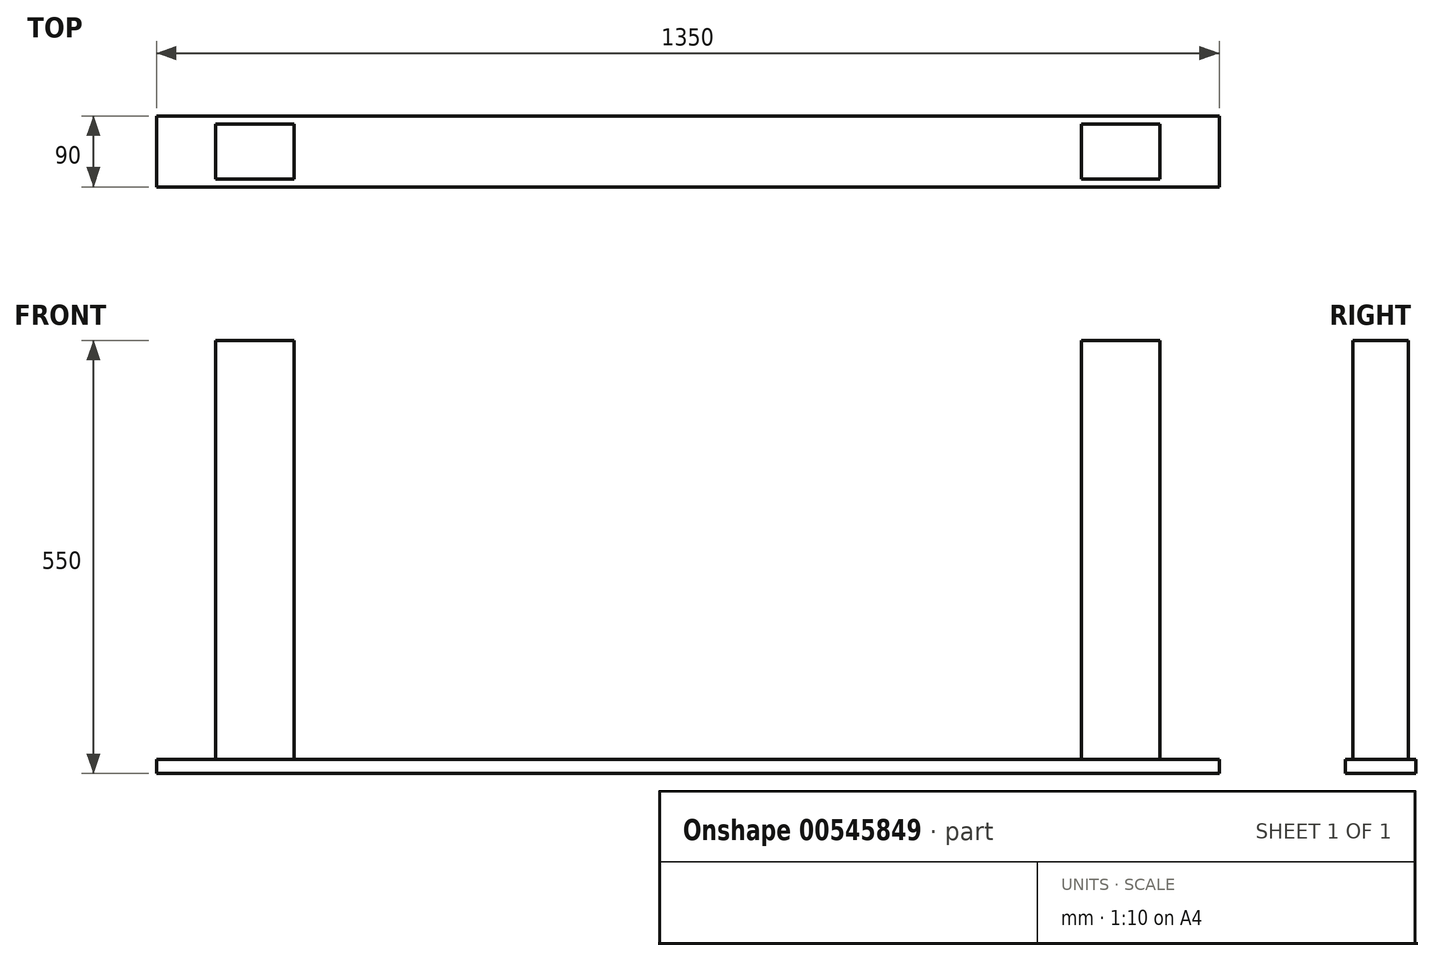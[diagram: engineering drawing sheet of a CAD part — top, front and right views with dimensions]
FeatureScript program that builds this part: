
annotation { "Feature Type Name" : "Feature", "Feature Type Description" : "" }
export const myFeature = defineFeature(function(context is Context, id is Id, definition is map)
    precondition{}
    {
        {
            var Q0;
            Q0=qCreatedBy(makeId("Top.planeOp"),FACE);
            var sketch = newSketch(context, id + "F0", { "sketchPlane" : qUnion([Q0])});
            skLineSegment(sketch, "E0", {"start": v(0, 0) * mm, "end": v(0, -1700) * mm, "construction": true});
            skLineSegment(sketch, "E1", {"start": v(-675, 0) * mm, "end": v(0, 0) * mm, "construction": true});
            skLineSegment(sketch, "E2", {"start": v(-675, -1350) * mm, "end": v(-675, -1700) * mm, "construction": true});
            skLineSegment(sketch, "E3", {"start": v(-675, -1700) * mm, "end": v(-425, -1700) * mm, "construction": true});
            skLineSegment(sketch, "E4.MirrorCS", {"start": v(675, 0) * mm, "end": v(0, 0) * mm, "construction": true});
            skLineSegment(sketch, "E5", {"start": v(-425, -1700) * mm, "end": v(-675, -1350) * mm, "construction": true});
            skLineSegment(sketch, "E6", {"start": v(675, 0) * mm, "end": v(675, -1350) * mm, "construction": true});
            skLineSegment(sketch, "E7", {"start": v(425, -1700) * mm, "end": v(-425, -1700) * mm, "construction": true});
            skLineSegment(sketch, "E8", {"start": v(675, -1350) * mm, "end": v(425, -1700) * mm, "construction": true});
            skLineSegment(sketch, "E9", {"start": v(-675, -1350) * mm, "end": v(-675, 0) * mm, "construction": true});
            skLineSegment(sketch, "E10", {"start": v(-675, -650) * mm, "end": v(675, -650) * mm, "construction": true});
            skLineSegment(sketch, "E11.bottom", {"start": v(-675, -325) * mm, "end": v(675, -325) * mm});
            skLineSegment(sketch, "E11.left", {"start": v(-675, -325) * mm, "end": v(-675, -415) * mm});
            skLineSegment(sketch, "E11.right", {"start": v(675, -325) * mm, "end": v(675, -650) * mm});
            skLineSegment(sketch, "E12", {"start": v(-675, -415) * mm, "end": v(675, -415) * mm});
            skLineSegment(sketch, "E13", {"start": v(675, -415) * mm, "end": v(675, -325) * mm});
            skSolve(sketch);
        }
        {
            var Q0;
            Q0=makeQuery(id+"F0.imprint","IMPRINT",FACE,{"disambiguationData":[TD([[makeQuery(id+"F0.imprint","IMPRINT",EDGE,{"derivedFrom":sQuery(id+"F0.wireOp",EDGE,"E11.bottom")}),-1.0]])]});
            extrude(context, id + "F1", {"entities" : qUnion([Q0]), "depth" : 18 * mm, "offsetDistance" : 25 * mm});
        }
        {
            var Q0;
            Q0=qCreatedBy(makeId("Top.planeOp"),FACE);
            var sketch = newSketch(context, id + "F2", { "sketchPlane" : qUnion([Q0])});
            skLineSegment(sketch, "E14.bottom", {"start": v(-600, -335) * mm, "end": v(-500, -335) * mm});
            skLineSegment(sketch, "E14.top", {"start": v(-600, -405) * mm, "end": v(-500, -405) * mm});
            skLineSegment(sketch, "E14.left", {"start": v(-600, -335) * mm, "end": v(-600, -405) * mm});
            skLineSegment(sketch, "E14.right", {"start": v(-500, -335) * mm, "end": v(-500, -405) * mm});
            skLineSegment(sketch, "E15", {"start": v(0, -120.6) * mm, "end": v(0, -735.07) * mm});
            skLineSegment(sketch, "E16.MirrorCS", {"start": v(600, -335) * mm, "end": v(500, -335) * mm});
            skLineSegment(sketch, "E17.MirrorCS", {"start": v(600, -335) * mm, "end": v(600, -405) * mm});
            skLineSegment(sketch, "E18.MirrorCS", {"start": v(600, -405) * mm, "end": v(500, -405) * mm});
            skLineSegment(sketch, "E19.MirrorCS", {"start": v(500, -335) * mm, "end": v(500, -405) * mm});
            skSolve(sketch);
        }
        {
            var Q0;
            Q0 = qSketchRegion(id + "F2", true);
            extrude(context, id + "F3", {"entities" : qUnion([Q0]), "operationType" : NewBodyOperationType.ADD, "depth" : 550 * mm, "offsetDistance" : 25 * mm});
        }
    });
